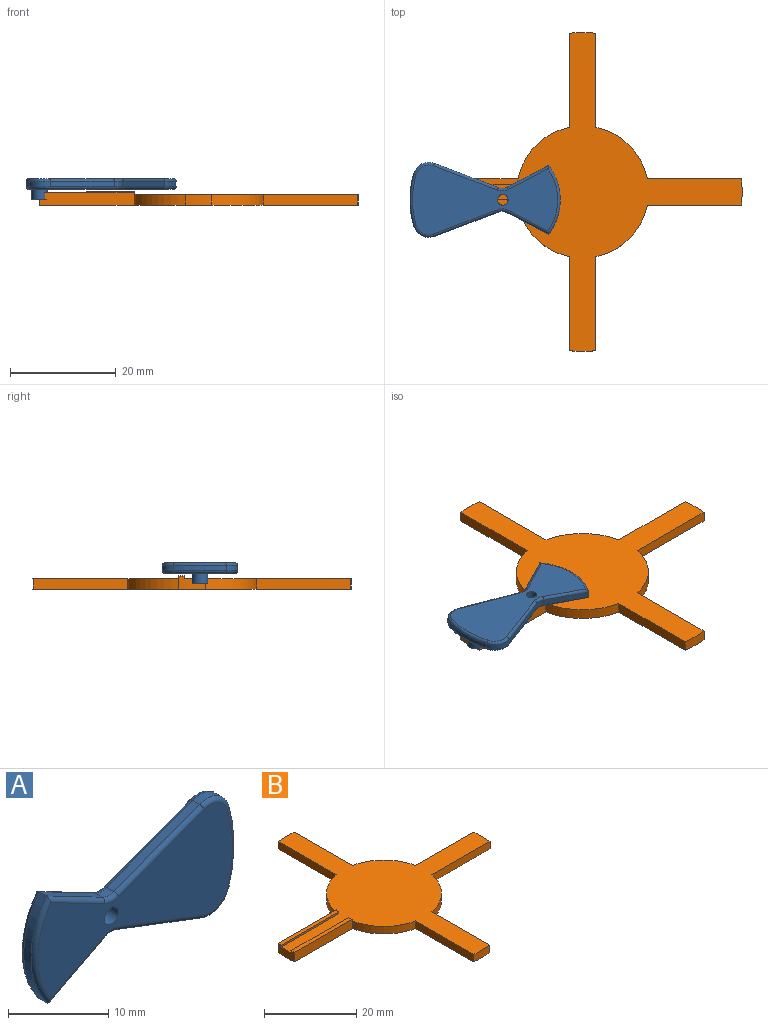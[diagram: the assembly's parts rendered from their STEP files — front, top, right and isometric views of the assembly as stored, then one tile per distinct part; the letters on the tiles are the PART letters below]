
ASSEMBLY  parts=2 mates=1
PART A: 35 faces, bbox 30.8x4x14.7 mm
  f0: cylinder r=2mm len=1.63mm, axis (0,1,0), area 1.7mm2, adj f1,f10,f17,f30
  f1: plane 7.92x4.12mm, normal (0.46,0,0.89), area 8.9mm2, adj f0,f2,f19,f32
  f2: cylinder r=10.89mm len=13.06mm, axis (0,1,0), area 14mm2, adj f1,f3,f21,f31
  f3: plane 7.92x4.12mm, normal (0.46,0,-0.89), area 8.9mm2, adj f2,f4,f22,f29
  f4: cylinder r=2mm len=1.63mm, axis (0,1,0), area 1.7mm2, adj f3,f5,f20,f27
  f5: plane 12.1x4.6mm, normal (-0.36,0,-0.93), area 12.9mm2, adj f4,f6,f18,f25
  f6: cylinder r=3mm len=3.94mm, axis (0,1,0), area 4.9mm2, adj f5,f7,f16,f23
  f7: cylinder r=17.59mm len=9.92mm, axis (0,1,0), area 10.1mm2, adj f6,f8,f14,f24
  f8: cylinder r=3mm len=3.94mm, axis (0,1,0), area 4.9mm2, adj f7,f10,f13,f26
  f9: cylinder r=1mm len=2mm, axis (0,1,0), area 12.6mm2, adj f11,f12
  f10: plane 12.1x4.6mm, normal (-0.36,0,0.93), area 12.9mm2, adj f0,f8,f15,f28
  f11: plane 27.48x13.23mm, normal (0,-1,0), area 223.9mm2, adj f9,f13,f14,f15,f16,f17,f18,f19
  f12: plane 27.48x13.23mm, normal (0,1,0), area 216.8mm2, adj f9,f23,f24,f25,f26,f27,f28,f29
  f13: torus R=2.5mm, axis (0,-1,0), area 3.6mm2, adj f8,f11,f14,f15
  f14: torus R=17.09mm, axis (0,-1,0), area 7.8mm2, adj f7,f11,f13,f16
  f15: cylinder r=0.5mm len=12.27mm, axis (0.93,0,0.36), area 10.2mm2, adj f10,f11,f13,f17
  f16: torus R=2.5mm, axis (0,-1,0), area 3.6mm2, adj f6,f11,f14,f18
  f17: torus R=2.5mm, axis (0,-1,0), area 1.4mm2, adj f0,f11,f15,f19
  f18: cylinder r=0.5mm len=12.27mm, axis (-0.93,0,0.36), area 10.2mm2, adj f5,f11,f16,f20
  f19: cylinder r=0.5mm len=8.15mm, axis (0.89,0,-0.46), area 6.9mm2, adj f1,f11,f17,f21
  f20: torus R=2.5mm, axis (0,-1,0), area 1.4mm2, adj f4,f11,f18,f22
  f21: torus R=10.39mm, axis (0,-1,0), area 10.6mm2, adj f2,f11,f19,f22
  f22: cylinder r=0.5mm len=8.15mm, axis (-0.89,0,-0.46), area 6.9mm2, adj f3,f11,f20,f21
  f23: torus R=2.5mm, axis (0,-1,0), area 3.6mm2, adj f6,f12,f24,f25
  f24: torus R=17.09mm, axis (0,-1,0), area 7.8mm2, adj f7,f12,f23,f26
  f25: cylinder r=0.5mm len=12.27mm, axis (0.93,0,-0.36), area 10.2mm2, adj f5,f12,f23,f27
  f26: torus R=2.5mm, axis (0,-1,0), area 3.6mm2, adj f8,f12,f24,f28
  f27: torus R=2.5mm, axis (0,-1,0), area 1.4mm2, adj f4,f12,f25,f29
  f28: cylinder r=0.5mm len=12.27mm, axis (-0.93,0,-0.36), area 10.2mm2, adj f10,f12,f26,f30
  f29: cylinder r=0.5mm len=8.15mm, axis (0.89,0,0.46), area 6.9mm2, adj f3,f12,f27,f31
  f30: torus R=2.5mm, axis (0,-1,0), area 1.4mm2, adj f0,f12,f28,f32
  f31: torus R=10.39mm, axis (0,-1,0), area 10.6mm2, adj f2,f12,f29,f32
  f32: cylinder r=0.5mm len=8.15mm, axis (-0.89,0,0.46), area 6.9mm2, adj f1,f12,f30,f31
  f33: cylinder r=1.5mm len=3mm, axis (0,-1,0), area 18.8mm2, adj f12,f34
  f34: plane 3x3mm, normal (0,1,0), area 7.1mm2, adj f33
PART B: 24 faces, bbox 60.4x60.4x2.5 mm
  f0: plane 60.36x60.36mm, normal (0,0,1), area 809.9mm2, adj f1,f2,f3,f4,f6,f7,f8,f11
  f1: cylinder r=12.5mm len=9.75mm, axis (0,0,-1), area 29.2mm2, adj f0,f5,f12,f15
  f2: cylinder r=12.5mm len=9.75mm, axis (0,0,-1), area 29.2mm2, adj f0,f5,f9,f13
  f3: cylinder r=12.5mm len=9.75mm, axis (0,0,-1), area 29.2mm2, adj f0,f5,f7,f10
  f4: cylinder r=12.5mm len=9.75mm, axis (0,0,-1), area 29.2mm2, adj f0,f5,f8,f17
  f5: plane 60.36x60.36mm, normal (0,0,-1), area 845.4mm2, adj f1,f2,f3,f4,f6,f7,f8,f9
  f6: cylinder r=30.18mm len=5mm, axis (0,0,-1), area 10mm2, adj f0,f5,f7,f8
  f7: plane 17.83x2mm, normal (-1,0,0), area 35.7mm2, adj f0,f3,f5,f6
  f8: plane 17.83x2mm, normal (1,0,0), area 35.7mm2, adj f0,f4,f5,f6
  f9: plane 17.83x2.5mm, normal (0,-1,0), area 44.6mm2, adj f2,f5,f11,f22,f23
  f10: plane 17.83x2.5mm, normal (0,1,0), area 44.6mm2, adj f3,f5,f11,f18,f20
  f11: cylinder r=30.18mm len=5mm, axis (0,0,-1), area 11mm2, adj f0,f5,f9,f10,f19,f20,f21,f23
  f12: plane 17.83x2mm, normal (1,0,0), area 35.7mm2, adj f0,f1,f5,f14
  f13: plane 17.83x2mm, normal (-1,0,0), area 35.7mm2, adj f0,f2,f5,f14
  f14: cylinder r=30.18mm len=5mm, axis (0,0,-1), area 10mm2, adj f0,f5,f12,f13
  f15: plane 17.83x2mm, normal (0,-1,0), area 35.7mm2, adj f0,f1,f5,f16
  f16: cylinder r=30.18mm len=5mm, axis (0,0,-1), area 10mm2, adj f0,f5,f15,f17
  f17: plane 17.83x2mm, normal (0,1,0), area 35.7mm2, adj f0,f4,f5,f16
  f18: cylinder r=12.5mm len=1mm, axis (0,0,-1), area 0.5mm2, adj f0,f10,f19,f20
  f19: plane 17.73x0.5mm, normal (0,-1,0), area 8.9mm2, adj f0,f11,f18,f20
  f20: plane 17.89x1mm, normal (0,0,1), area 17.8mm2, adj f10,f11,f18,f19
  f21: plane 17.73x0.5mm, normal (0,1,0), area 8.9mm2, adj f0,f11,f22,f23
  f22: cylinder r=12.5mm len=1mm, axis (0,0,-1), area 0.5mm2, adj f0,f9,f21,f23
  f23: plane 17.89x1mm, normal (0,0,1), area 17.8mm2, adj f9,f11,f21,f22
PLACE A rot(axis=(0,0.71,-0.71),180deg) t=(-60.49,-28.24,32.81)mm
PLACE B t=(-45.35,-26.74,30.81)mm
MATE slider A.f33 <-> B.f0  axis (0,0,1) through (-75.49,-28.24,31.81)mm
